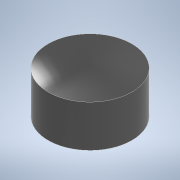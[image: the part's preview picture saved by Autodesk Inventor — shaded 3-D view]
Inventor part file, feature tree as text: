
AUTODESK INVENTOR PART (.ipt)
format: ipt  version: 2021 (Build 250183000, 183)  size: 123,904 bytes
history: native  units: mm
features: revolve x1, sketch x1
ambient origin geometry x8: Origin, YZ Plane, XZ Plane, XY Plane, X Axis, Y Axis, Z Axis, Center Point
bodies: Solid1 (feature_tree)
feature tree (2):
  revolve  "Revolution1"  [1 undecoded]
  sketch  "Sketch1"  dims[d0=20.0mm d1=23.0mm d2=0.0mm d3=21.0mm d5=25.0mm d6=90.0deg d7=23.0mm]
note: 1 required parameter value undecoded (feature->parameter linkage not recoverable at this tier; creation-order binding heuristic only, values carry confidence <= 0.55)
